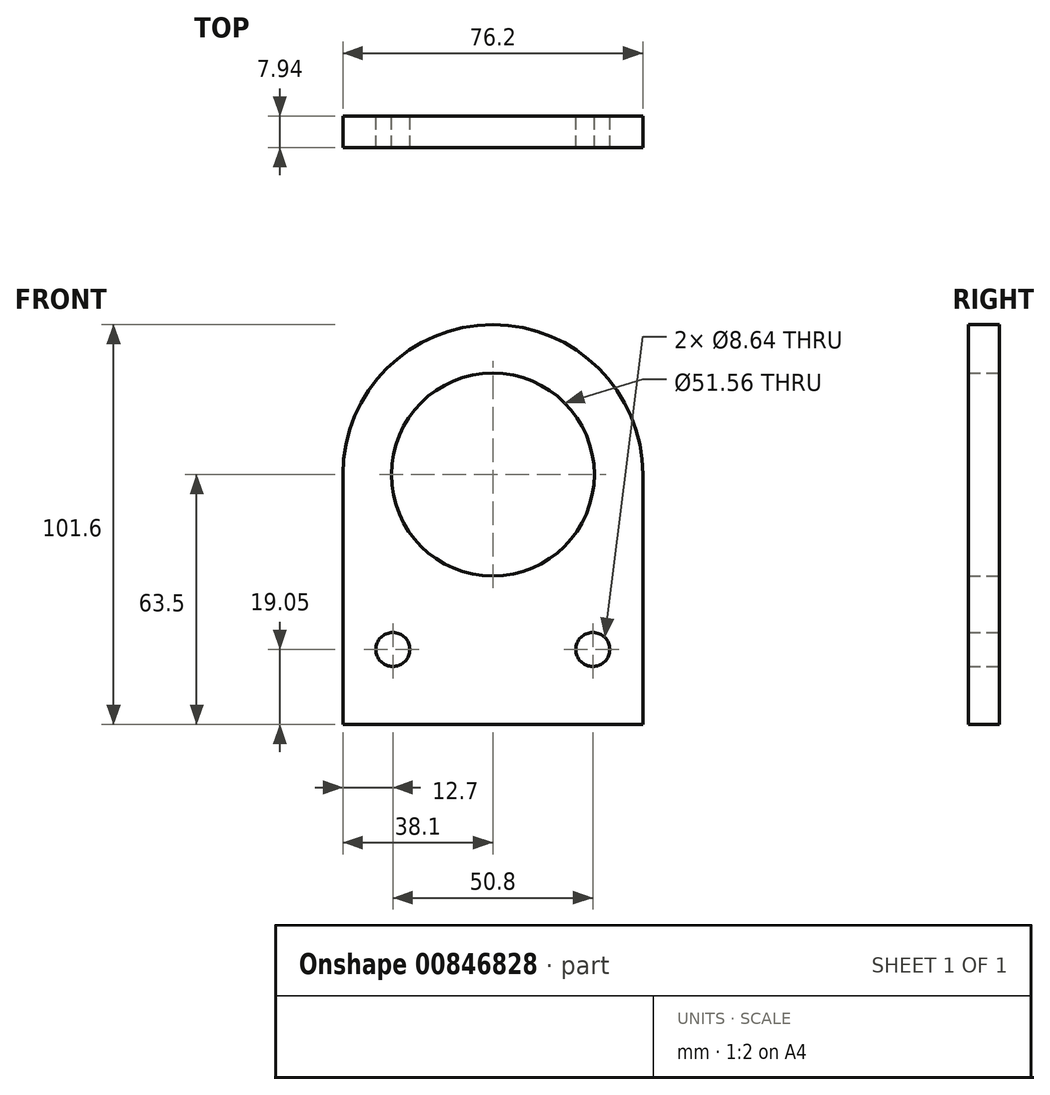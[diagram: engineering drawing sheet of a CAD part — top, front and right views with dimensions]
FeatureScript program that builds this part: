
annotation { "Feature Type Name" : "Feature", "Feature Type Description" : "" }
export const myFeature = defineFeature(function(context is Context, id is Id, definition is map)
    precondition{}
    {
        {
            var Q0;
            Q0=qCreatedBy(makeId("Front.planeOp"),FACE);
            var sketch = newSketch(context, id + "F0", { "sketchPlane" : qUnion([Q0])});
            skCircle(sketch, "E0", {"center": v(0, 0) * mm, "radius": 25.78 * mm});
            skArc(sketch, "E1", {"start": v(38.1, 0) * mm, "mid": v(0, 38.1) * mm, "end": v(-38.1, 0) * mm});
            skLineSegment(sketch, "E2.top", {"start": v(-38.1, -63.5) * mm, "end": v(38.1, -63.5) * mm});
            skLineSegment(sketch, "E2.left", {"start": v(-38.1, 0) * mm, "end": v(-38.1, -63.5) * mm});
            skLineSegment(sketch, "E2.right", {"start": v(38.1, 0) * mm, "end": v(38.1, -63.5) * mm});
            skLineSegment(sketch, "E3", {"start": v(-25.4, -44.45) * mm, "end": v(25.4, -44.45) * mm, "construction": true});
            skLineSegment(sketch, "E4", {"start": v(0, 0) * mm, "end": v(0, -44.45) * mm, "construction": true});
            skCircle(sketch, "E5", {"center": v(-25.4, -44.45) * mm, "radius": 4.32 * mm});
            skCircle(sketch, "E6", {"center": v(25.4, -44.45) * mm, "radius": 4.32 * mm});
            skSolve(sketch);
        }
        {
            var Q0;
            Q0 = qSketchRegion(id + "F0", true);
            extrude(context, id + "F1", {"entities" : qUnion([Q0]), "depth" : 7.94 * mm, "offsetDistance" : 25.4 * mm});
        }
    });
